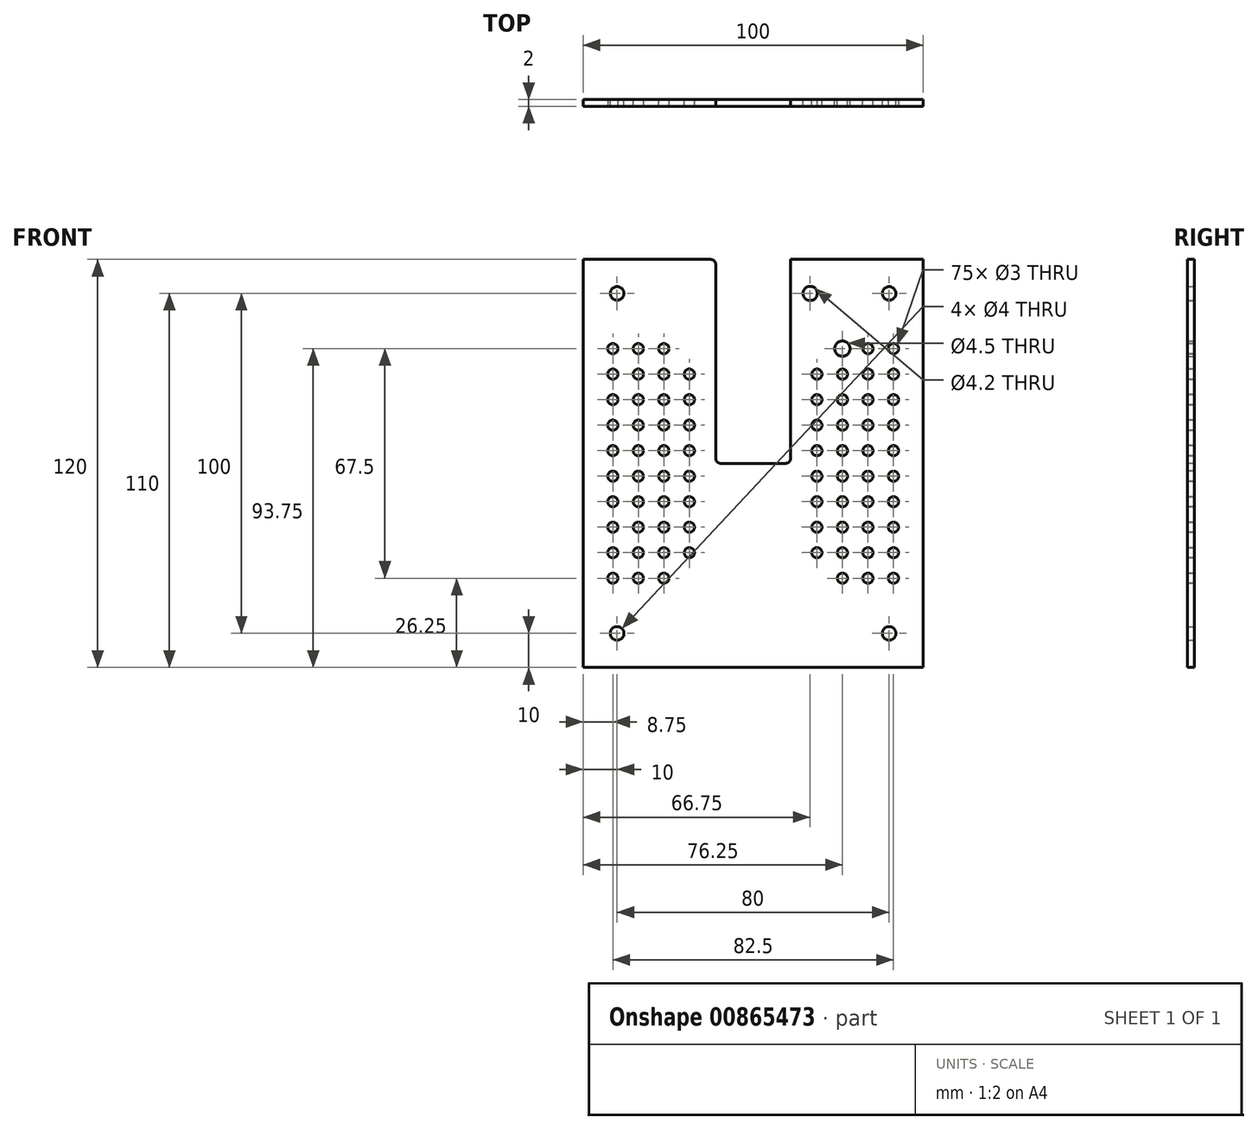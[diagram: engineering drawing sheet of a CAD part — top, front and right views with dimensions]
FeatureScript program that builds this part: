
annotation { "Feature Type Name" : "Feature", "Feature Type Description" : "" }
export const myFeature = defineFeature(function(context is Context, id is Id, definition is map)
    precondition{}
    {
        {
            var Q0;
            Q0=qCreatedBy(makeId("Front.planeOp"),FACE);
            var sketch = newSketch(context, id + "F0", { "sketchPlane" : qUnion([Q0])});
            skLineSegment(sketch, "E0.bottom", {"start": v(50, 60) * mm, "end": v(-50, 60) * mm});
            skLineSegment(sketch, "E0.top", {"start": v(50, -60) * mm, "end": v(-50, -60) * mm});
            skLineSegment(sketch, "E0.left", {"start": v(50, 60) * mm, "end": v(50, -60) * mm});
            skLineSegment(sketch, "E0.right", {"start": v(-50, 60) * mm, "end": v(-50, -60) * mm});
            skPoint(sketch, "E0.middle", {"position": v(0, 0) * mm});
            skCircle(sketch, "E1", {"center": v(-40, 50) * mm, "radius": 2 * mm});
            skCircle(sketch, "E2", {"center": v(40, 50) * mm, "radius": 2 * mm});
            skCircle(sketch, "E3", {"center": v(40, -50) * mm, "radius": 2 * mm});
            skCircle(sketch, "E4", {"center": v(-40, -50) * mm, "radius": 2 * mm});
            skSolve(sketch);
        }
        {
            var Q0;
            Q0=qSketchRegion(id+"F0",true);
            extrude(context, id + "F1", {"entities" : qUnion([Q0]), "depth" : 2 * mm, "offsetDistance" : 25 * mm});
        }
        {
            var Q0;
            Q0=makeQuery(id+"F1.opExtrude","CAP_FACE",FACE,{"disambiguationData":[OSD([sQuery(id+"F0.wireOp",EDGE,"E0.bottom"),sQuery(id+"F0.wireOp",EDGE,"E0.top"),sQuery(id+"F0.wireOp",EDGE,"E0.left"),sQuery(id+"F0.wireOp",EDGE,"E0.right"),sQuery(id+"F0.wireOp",EDGE,"E1"),sQuery(id+"F0.wireOp",EDGE,"E2"),sQuery(id+"F0.wireOp",EDGE,"E3"),sQuery(id+"F0.wireOp",EDGE,"E4")])],"isStart":false});
            var sketch = newSketch(context, id + "F2", { "sketchPlane" : qUnion([Q0])});
            skLineSegment(sketch, "E5.bottom", {"start": v(11, 60) * mm, "end": v(-11, 60) * mm});
            skLineSegment(sketch, "E5.top", {"start": v(11, 0) * mm, "end": v(-11, 0) * mm});
            skLineSegment(sketch, "E5.left", {"start": v(11, 60) * mm, "end": v(11, 0) * mm});
            skLineSegment(sketch, "E5.right", {"start": v(-11, 60) * mm, "end": v(-11, 0) * mm});
            skPoint(sketch, "E5.middle", {"position": v(0, 30) * mm});
            skSolve(sketch);
        }
        {
            var Q0;
            Q0 = qSketchRegion(id + "F2", true);
            extrude(context, id + "F3", {"entities" : qUnion([Q0]), "operationType" : NewBodyOperationType.REMOVE, "endBound" : BoundingType.THROUGH_ALL, "oppositeDirection" : true, "depth" : 25 * mm, "offsetDistance" : 25 * mm});
        }
        {
            var Q0;
            Q0=makeQuery(id+"F3.boolean.opBoolean","COPY",EDGE,{"derivedFrom":makeQuery(id+"F3.opExtrude","SWEPT_EDGE",EDGE,{"disambiguationData":[OSD([sQuery(id+"F2.wireOp",EDGE,"E5.top"),sQuery(id+"F2.wireOp",EDGE,"E5.right")])]})});
            var Q1;
            Q1=makeQuery(id+"F3.boolean.opBoolean","COPY",EDGE,{"derivedFrom":makeQuery(id+"F3.opExtrude","SWEPT_EDGE",EDGE,{"disambiguationData":[OSD([sQuery(id+"F2.wireOp",EDGE,"E5.top"),sQuery(id+"F2.wireOp",EDGE,"E5.left")])]})});
            var Q2;
            Q2=makeQuery(id+"F3.boolean.opBoolean","COPY",EDGE,{"derivedFrom":makeQuery(id+"F3.opExtrude","SWEPT_EDGE",EDGE,{"disambiguationData":[OSD([sQuery(id+"F0.wireOp",EDGE,"E0.bottom"),sQuery(id+"F2.wireOp",EDGE,"E5.bottom"),sQuery(id+"F2.wireOp",EDGE,"E5.right")])]})});
            var Q3;
            Q3=makeQuery(id+"F3.boolean.opBoolean","COPY",EDGE,{"derivedFrom":makeQuery(id+"F3.opExtrude","SWEPT_EDGE",EDGE,{"disambiguationData":[OSD([sQuery(id+"F0.wireOp",EDGE,"E0.bottom"),sQuery(id+"F2.wireOp",EDGE,"E5.bottom"),sQuery(id+"F2.wireOp",EDGE,"E5.left")])]})});
            fillet(context, id + "F4", {"entities" : qUnion([Q0, Q1, Q2, Q3]), "radius" : 1.5 * mm, "tangentPropagation" : true, "allowEdgeOverflow" : false});
        }
        {
            var Q0;
            Q0=makeQuery(id+"F1.opExtrude","CAP_FACE",FACE,{"disambiguationData":[OSD([sQuery(id+"F0.wireOp",EDGE,"E0.bottom"),sQuery(id+"F0.wireOp",EDGE,"E0.top"),sQuery(id+"F0.wireOp",EDGE,"E0.left"),sQuery(id+"F0.wireOp",EDGE,"E0.right"),sQuery(id+"F0.wireOp",EDGE,"E1"),sQuery(id+"F0.wireOp",EDGE,"E2"),sQuery(id+"F0.wireOp",EDGE,"E3"),sQuery(id+"F0.wireOp",EDGE,"E4")])],"isStart":true});
            var sketch = newSketch(context, id + "F5", { "sketchPlane" : qUnion([Q0])});
            skCircle(sketch, "E6", {"center": v(33.75, 33.75) * mm, "radius": 1.5 * mm});
            skCircle(sketch, "E7.0.1.0", {"center": v(33.75, 26.25) * mm, "radius": 1.5 * mm});
            skCircle(sketch, "E7.0.2.0", {"center": v(33.75, 18.75) * mm, "radius": 1.5 * mm});
            skCircle(sketch, "E7.0.3.0", {"center": v(33.75, 11.25) * mm, "radius": 1.5 * mm});
            skCircle(sketch, "E7.0.4.0", {"center": v(33.75, 3.75) * mm, "radius": 1.5 * mm});
            skCircle(sketch, "E7.0.5.0", {"center": v(33.75, -3.75) * mm, "radius": 1.5 * mm});
            skCircle(sketch, "E7.0.6.0", {"center": v(33.75, -11.25) * mm, "radius": 1.5 * mm});
            skCircle(sketch, "E7.0.7.0", {"center": v(33.75, -18.75) * mm, "radius": 1.5 * mm});
            skCircle(sketch, "E7.0.8.0", {"center": v(33.75, -26.25) * mm, "radius": 1.5 * mm});
            skCircle(sketch, "E7.0.9.0", {"center": v(33.75, -33.75) * mm, "radius": 1.5 * mm});
            skCircle(sketch, "E7.1.0.0", {"center": v(26.25, 33.75) * mm, "radius": 1.5 * mm});
            skCircle(sketch, "E7.1.1.0", {"center": v(26.25, 26.25) * mm, "radius": 1.5 * mm});
            skCircle(sketch, "E7.1.2.0", {"center": v(26.25, 18.75) * mm, "radius": 1.5 * mm});
            skCircle(sketch, "E7.1.3.0", {"center": v(26.25, 11.25) * mm, "radius": 1.5 * mm});
            skCircle(sketch, "E7.1.4.0", {"center": v(26.25, 3.75) * mm, "radius": 1.5 * mm});
            skCircle(sketch, "E7.1.5.0", {"center": v(26.25, -3.75) * mm, "radius": 1.5 * mm});
            skCircle(sketch, "E7.1.6.0", {"center": v(26.25, -11.25) * mm, "radius": 1.5 * mm});
            skCircle(sketch, "E7.1.7.0", {"center": v(26.25, -18.75) * mm, "radius": 1.5 * mm});
            skCircle(sketch, "E7.1.8.0", {"center": v(26.25, -26.25) * mm, "radius": 1.5 * mm});
            skCircle(sketch, "E7.1.9.0", {"center": v(26.25, -33.75) * mm, "radius": 1.5 * mm});
            skCircle(sketch, "E7.2.1.0", {"center": v(18.75, 26.25) * mm, "radius": 1.5 * mm});
            skCircle(sketch, "E7.2.2.0", {"center": v(18.75, 18.75) * mm, "radius": 1.5 * mm});
            skCircle(sketch, "E7.2.3.0", {"center": v(18.75, 11.25) * mm, "radius": 1.5 * mm});
            skCircle(sketch, "E7.2.4.0", {"center": v(18.75, 3.75) * mm, "radius": 1.5 * mm});
            skCircle(sketch, "E7.2.5.0", {"center": v(18.75, -3.75) * mm, "radius": 1.5 * mm});
            skCircle(sketch, "E7.2.6.0", {"center": v(18.75, -11.25) * mm, "radius": 1.5 * mm});
            skCircle(sketch, "E7.2.7.0", {"center": v(18.75, -18.75) * mm, "radius": 1.5 * mm});
            skCircle(sketch, "E7.2.8.0", {"center": v(18.75, -26.25) * mm, "radius": 1.5 * mm});
            skLineSegment(sketch, "E7.direction1", {"start": v(40, 40) * mm, "end": v(32.5, 40) * mm, "construction": true});
            skLineSegment(sketch, "E7.direction2", {"start": v(40, 40) * mm, "end": v(40, 32.5) * mm, "construction": true});
            skCircle(sketch, "E8.MirrorC", {"center": v(-26.25, 18.75) * mm, "radius": 1.5 * mm});
            skCircle(sketch, "E9.MirrorC", {"center": v(-26.25, 3.75) * mm, "radius": 1.5 * mm});
            skCircle(sketch, "E10.MirrorC", {"center": v(-18.75, -18.75) * mm, "radius": 1.5 * mm});
            skCircle(sketch, "E11.MirrorC", {"center": v(-33.75, -26.25) * mm, "radius": 1.5 * mm});
            skCircle(sketch, "E12.MirrorC", {"center": v(-33.75, 18.75) * mm, "radius": 1.5 * mm});
            skCircle(sketch, "E13.MirrorC", {"center": v(-26.25, 26.25) * mm, "radius": 1.5 * mm});
            skCircle(sketch, "E14.MirrorC", {"center": v(-26.25, 33.75) * mm, "radius": 1.5 * mm});
            skCircle(sketch, "E15.MirrorC", {"center": v(-33.75, 33.75) * mm, "radius": 1.5 * mm});
            skCircle(sketch, "E16.MirrorC", {"center": v(-18.75, 3.75) * mm, "radius": 1.5 * mm});
            skCircle(sketch, "E17.MirrorC", {"center": v(-33.75, 3.75) * mm, "radius": 1.5 * mm});
            skCircle(sketch, "E18.MirrorC", {"center": v(-26.25, -3.75) * mm, "radius": 1.5 * mm});
            skCircle(sketch, "E19.MirrorC", {"center": v(-33.75, -33.75) * mm, "radius": 1.5 * mm});
            skCircle(sketch, "E20.MirrorC", {"center": v(-26.25, -26.25) * mm, "radius": 1.5 * mm});
            skCircle(sketch, "E21.MirrorC", {"center": v(-33.75, -11.25) * mm, "radius": 1.5 * mm});
            skCircle(sketch, "E22.MirrorC", {"center": v(-26.25, -11.25) * mm, "radius": 1.5 * mm});
            skCircle(sketch, "E23.MirrorC", {"center": v(-33.75, -3.75) * mm, "radius": 1.5 * mm});
            skCircle(sketch, "E24.MirrorC", {"center": v(-33.75, 26.25) * mm, "radius": 1.5 * mm});
            skCircle(sketch, "E25.MirrorC", {"center": v(-18.75, 11.25) * mm, "radius": 1.5 * mm});
            skCircle(sketch, "E26.MirrorC", {"center": v(-18.75, 18.75) * mm, "radius": 1.5 * mm});
            skCircle(sketch, "E27.MirrorC", {"center": v(-18.75, -11.25) * mm, "radius": 1.5 * mm});
            skCircle(sketch, "E28.MirrorC", {"center": v(-18.75, 26.25) * mm, "radius": 1.5 * mm});
            skCircle(sketch, "E29.MirrorC", {"center": v(-26.25, -18.75) * mm, "radius": 1.5 * mm});
            skCircle(sketch, "E30.MirrorC", {"center": v(-33.75, -18.75) * mm, "radius": 1.5 * mm});
            skCircle(sketch, "E31.MirrorC", {"center": v(-26.25, 11.25) * mm, "radius": 1.5 * mm});
            skCircle(sketch, "E32.MirrorC", {"center": v(-18.75, -26.25) * mm, "radius": 1.5 * mm});
            skCircle(sketch, "E33.MirrorC", {"center": v(-33.75, 11.25) * mm, "radius": 1.5 * mm});
            skCircle(sketch, "E34.MirrorC", {"center": v(-18.75, -3.75) * mm, "radius": 1.5 * mm});
            skCircle(sketch, "E35.MirrorC", {"center": v(-26.25, -33.75) * mm, "radius": 1.5 * mm});
            skSolve(sketch);
        }
        {
            var Q0;
            Q0 = qSketchRegion(id + "F5", true);
            extrude(context, id + "F6", {"entities" : qUnion([Q0]), "operationType" : NewBodyOperationType.REMOVE, "endBound" : BoundingType.THROUGH_ALL, "oppositeDirection" : true, "depth" : 25 * mm, "offsetDistance" : 25 * mm});
        }
        {
            var Q0;
            Q0=makeQuery(id+"F1.opExtrude","CAP_FACE",FACE,{"disambiguationData":[OSD([sQuery(id+"F0.wireOp",EDGE,"E0.bottom"),sQuery(id+"F0.wireOp",EDGE,"E0.top"),sQuery(id+"F0.wireOp",EDGE,"E0.left"),sQuery(id+"F0.wireOp",EDGE,"E0.right"),sQuery(id+"F0.wireOp",EDGE,"E1"),sQuery(id+"F0.wireOp",EDGE,"E2"),sQuery(id+"F0.wireOp",EDGE,"E3"),sQuery(id+"F0.wireOp",EDGE,"E4")])],"isStart":false});
            var sketch = newSketch(context, id + "F7", { "sketchPlane" : qUnion([Q0])});
            skCircle(sketch, "E36.0.1.0", {"center": v(-41.25, 33.75) * mm, "radius": 1.5 * mm});
            skCircle(sketch, "E36.0.2.0", {"center": v(-41.25, 26.25) * mm, "radius": 1.5 * mm});
            skCircle(sketch, "E36.0.3.0", {"center": v(-41.25, 18.75) * mm, "radius": 1.5 * mm});
            skCircle(sketch, "E36.0.4.0", {"center": v(-41.25, 11.25) * mm, "radius": 1.5 * mm});
            skCircle(sketch, "E36.0.5.0", {"center": v(-41.25, 3.75) * mm, "radius": 1.5 * mm});
            skCircle(sketch, "E36.0.6.0", {"center": v(-41.25, -3.75) * mm, "radius": 1.5 * mm});
            skCircle(sketch, "E36.0.7.0", {"center": v(-41.25, -11.25) * mm, "radius": 1.5 * mm});
            skCircle(sketch, "E36.0.8.0", {"center": v(-41.25, -18.75) * mm, "radius": 1.5 * mm});
            skCircle(sketch, "E36.0.9.0", {"center": v(-41.25, -26.25) * mm, "radius": 1.5 * mm});
            skCircle(sketch, "E36.0.10.0", {"center": v(-41.25, -33.75) * mm, "radius": 1.5 * mm});
            skLineSegment(sketch, "E36.direction2", {"start": v(-41.25, 41.25) * mm, "end": v(-41.25, 33.75) * mm, "construction": true});
            skCircle(sketch, "E37.MirrorC", {"center": v(41.25, -26.25) * mm, "radius": 1.5 * mm});
            skCircle(sketch, "E38.MirrorC", {"center": v(41.25, -18.75) * mm, "radius": 1.5 * mm});
            skLineSegment(sketch, "E39.MirrorCS", {"start": v(41.25, 41.25) * mm, "end": v(41.25, 33.75) * mm, "construction": true});
            skCircle(sketch, "E40.MirrorC", {"center": v(41.25, -11.25) * mm, "radius": 1.5 * mm});
            skCircle(sketch, "E41.MirrorC", {"center": v(41.25, 18.75) * mm, "radius": 1.5 * mm});
            skCircle(sketch, "E42.MirrorC", {"center": v(41.25, -3.75) * mm, "radius": 1.5 * mm});
            skCircle(sketch, "E43.MirrorC", {"center": v(41.25, 26.25) * mm, "radius": 1.5 * mm});
            skCircle(sketch, "E44.MirrorC", {"center": v(41.25, 33.75) * mm, "radius": 1.5 * mm});
            skCircle(sketch, "E45.MirrorC", {"center": v(41.25, 3.75) * mm, "radius": 1.5 * mm});
            skCircle(sketch, "E46.MirrorC", {"center": v(41.25, 11.25) * mm, "radius": 1.5 * mm});
            skCircle(sketch, "E47.MirrorC", {"center": v(41.25, -33.75) * mm, "radius": 1.5 * mm});
            skPoint(sketch, "E36.0.11.0.center.orphan", {"position": v(-41.25, -41.25) * mm});
            skSolve(sketch);
        }
        {
            var Q0;
            Q0 = qSketchRegion(id + "F7", true);
            extrude(context, id + "F8", {"entities" : qUnion([Q0]), "operationType" : NewBodyOperationType.REMOVE, "endBound" : BoundingType.THROUGH_ALL, "oppositeDirection" : true, "depth" : 25 * mm, "offsetDistance" : 25 * mm});
        }
        {
            var Q0;
            Q0=makeQuery(id+"F1.opExtrude","CAP_FACE",FACE,{"disambiguationData":[OSD([sQuery(id+"F0.wireOp",EDGE,"E0.bottom"),sQuery(id+"F0.wireOp",EDGE,"E0.top"),sQuery(id+"F0.wireOp",EDGE,"E0.left"),sQuery(id+"F0.wireOp",EDGE,"E0.right"),sQuery(id+"F0.wireOp",EDGE,"E1"),sQuery(id+"F0.wireOp",EDGE,"E2"),sQuery(id+"F0.wireOp",EDGE,"E3"),sQuery(id+"F0.wireOp",EDGE,"E4")])],"isStart":true});
            var sketch = newSketch(context, id + "F9", { "sketchPlane" : qUnion([Q0])});
            skCircle(sketch, "E48", {"center": v(-26.25, 33.75) * mm, "radius": 2.25 * mm});
            skSolve(sketch);
        }
        {
            var Q0;
            Q0 = qSketchRegion(id + "F9", true);
            extrude(context, id + "F10", {"entities" : qUnion([Q0]), "operationType" : NewBodyOperationType.REMOVE, "endBound" : BoundingType.THROUGH_ALL, "oppositeDirection" : true, "depth" : 25 * mm, "offsetDistance" : 25 * mm});
        }
        {
            var Q0;
            Q0=makeQuery(id+"F1.opExtrude","CAP_FACE",FACE,{"disambiguationData":[OSD([sQuery(id+"F0.wireOp",EDGE,"E0.bottom"),sQuery(id+"F0.wireOp",EDGE,"E0.top"),sQuery(id+"F0.wireOp",EDGE,"E0.left"),sQuery(id+"F0.wireOp",EDGE,"E0.right"),sQuery(id+"F0.wireOp",EDGE,"E1"),sQuery(id+"F0.wireOp",EDGE,"E2"),sQuery(id+"F0.wireOp",EDGE,"E3"),sQuery(id+"F0.wireOp",EDGE,"E4")])],"isStart":true});
            var sketch = newSketch(context, id + "F11", { "sketchPlane" : qUnion([Q0])});
            skCircle(sketch, "E49", {"center": v(-16.75, 50) * mm, "radius": 2.1 * mm});
            skLineSegment(sketch, "E50", {"start": v(-40, 50) * mm, "end": v(-18.02, 50) * mm});
            skLineSegment(sketch, "E51", {"start": v(-26.25, 33.75) * mm, "end": v(-26.25, 56.8) * mm});
            skSolve(sketch);
        }
        {
            var Q0;
            Q0 = qSketchRegion(id + "F11", true);
            extrude(context, id + "F12", {"entities" : qUnion([Q0]), "operationType" : NewBodyOperationType.REMOVE, "endBound" : BoundingType.THROUGH_ALL, "oppositeDirection" : true, "depth" : 25 * mm, "offsetDistance" : 25 * mm});
        }
    });
